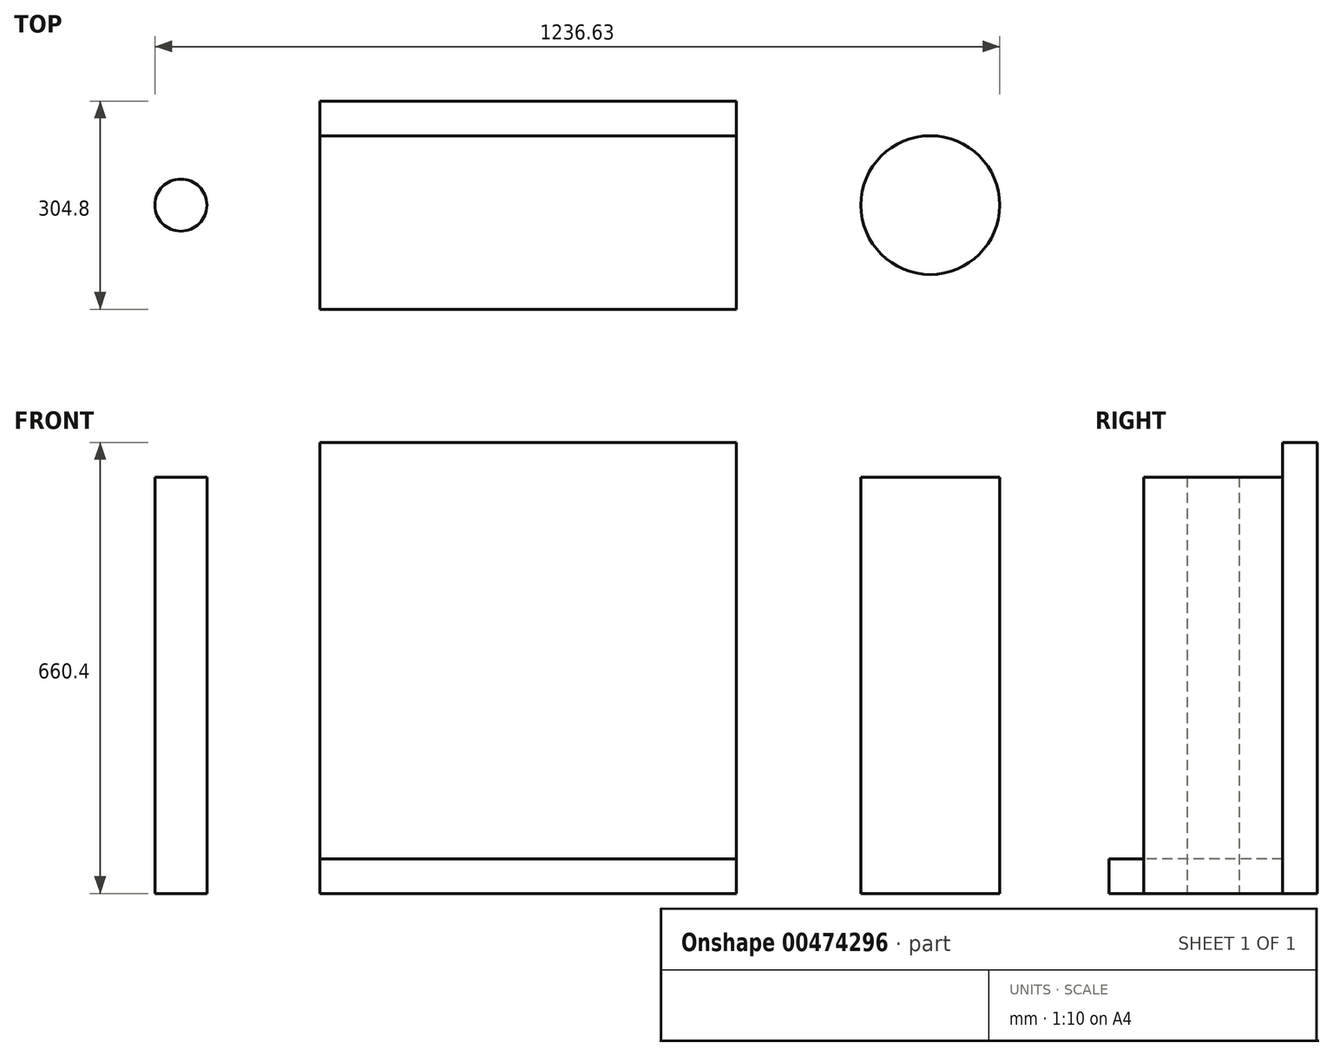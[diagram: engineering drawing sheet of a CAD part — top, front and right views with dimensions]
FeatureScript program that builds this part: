
annotation { "Feature Type Name" : "Feature", "Feature Type Description" : "" }
export const myFeature = defineFeature(function(context is Context, id is Id, definition is map)
    precondition{}
    {
        {
            var Q0;
            Q0=qCreatedBy(makeId("Top.planeOp"),FACE);
            var sketch = newSketch(context, id + "F0", { "sketchPlane" : qUnion([Q0])});
            skLineSegment(sketch, "E0.bottom", {"start": v(-304.8, 152.4) * mm, "end": v(304.8, 152.4) * mm});
            skLineSegment(sketch, "E0.top", {"start": v(-304.8, -152.4) * mm, "end": v(304.8, -152.4) * mm});
            skLineSegment(sketch, "E0.left", {"start": v(-304.8, 152.4) * mm, "end": v(-304.8, -152.4) * mm});
            skLineSegment(sketch, "E0.right", {"start": v(304.8, 152.4) * mm, "end": v(304.8, -152.4) * mm});
            skPoint(sketch, "E0.middle", {"position": v(0, 0) * mm});
            skSolve(sketch);
        }
        {
            var Q0;
            Q0 = qSketchRegion(id + "F0", true);
            extrude(context, id + "F1", {"entities" : qUnion([Q0]), "depth" : 50.8 * mm});
        }
        {
            var Q0;
            Q0=makeQuery(id+"F1.opExtrude","CAP_FACE",FACE,{"disambiguationData":[OSD([sQuery(id+"F0.wireOp",EDGE,"E0.bottom"),sQuery(id+"F0.wireOp",EDGE,"E0.top"),sQuery(id+"F0.wireOp",EDGE,"E0.left"),sQuery(id+"F0.wireOp",EDGE,"E0.right")])],"isStart":false});
            var sketch = newSketch(context, id + "F2", { "sketchPlane" : qUnion([Q0])});
            skLineSegment(sketch, "E1.bottom", {"start": v(-304.8, 152.4) * mm, "end": v(304.8, 152.4) * mm});
            skLineSegment(sketch, "E1.top", {"start": v(-304.8, 101.6) * mm, "end": v(304.8, 101.6) * mm});
            skLineSegment(sketch, "E1.left", {"start": v(-304.8, 152.4) * mm, "end": v(-304.8, 101.6) * mm});
            skLineSegment(sketch, "E1.right", {"start": v(304.8, 152.4) * mm, "end": v(304.8, 101.6) * mm});
            skSolve(sketch);
        }
        {
            var Q0;
            Q0 = qSketchRegion(id + "F2", true);
            extrude(context, id + "F3", {"entities" : qUnion([Q0]), "operationType" : NewBodyOperationType.ADD, "depth" : 609.6 * mm});
        }
        {
            var Q0;
            Q0=qCreatedBy(makeId("Top.planeOp"),FACE);
            var sketch = newSketch(context, id + "F4", { "sketchPlane" : qUnion([Q0])});
            skCircle(sketch, "E2", {"center": v(588.93, 0) * mm, "radius": 101.6 * mm});
            skSolve(sketch);
        }
        {
            var Q0;
            Q0 = qSketchRegion(id + "F4", true);
            extrude(context, id + "F5", {"entities" : qUnion([Q0]), "depth" : 609.6 * mm});
        }
        {
            var Q0;
            Q0=qCreatedBy(makeId("Top.planeOp"),FACE);
            var sketch = newSketch(context, id + "F6", { "sketchPlane" : qUnion([Q0])});
            skCircle(sketch, "E3", {"center": v(-508, 0) * mm, "radius": 38.1 * mm});
            skSolve(sketch);
        }
        {
            var Q0;
            Q0 = qSketchRegion(id + "F6", true);
            extrude(context, id + "F7", {"entities" : qUnion([Q0]), "depth" : 609.6 * mm});
        }
    });
